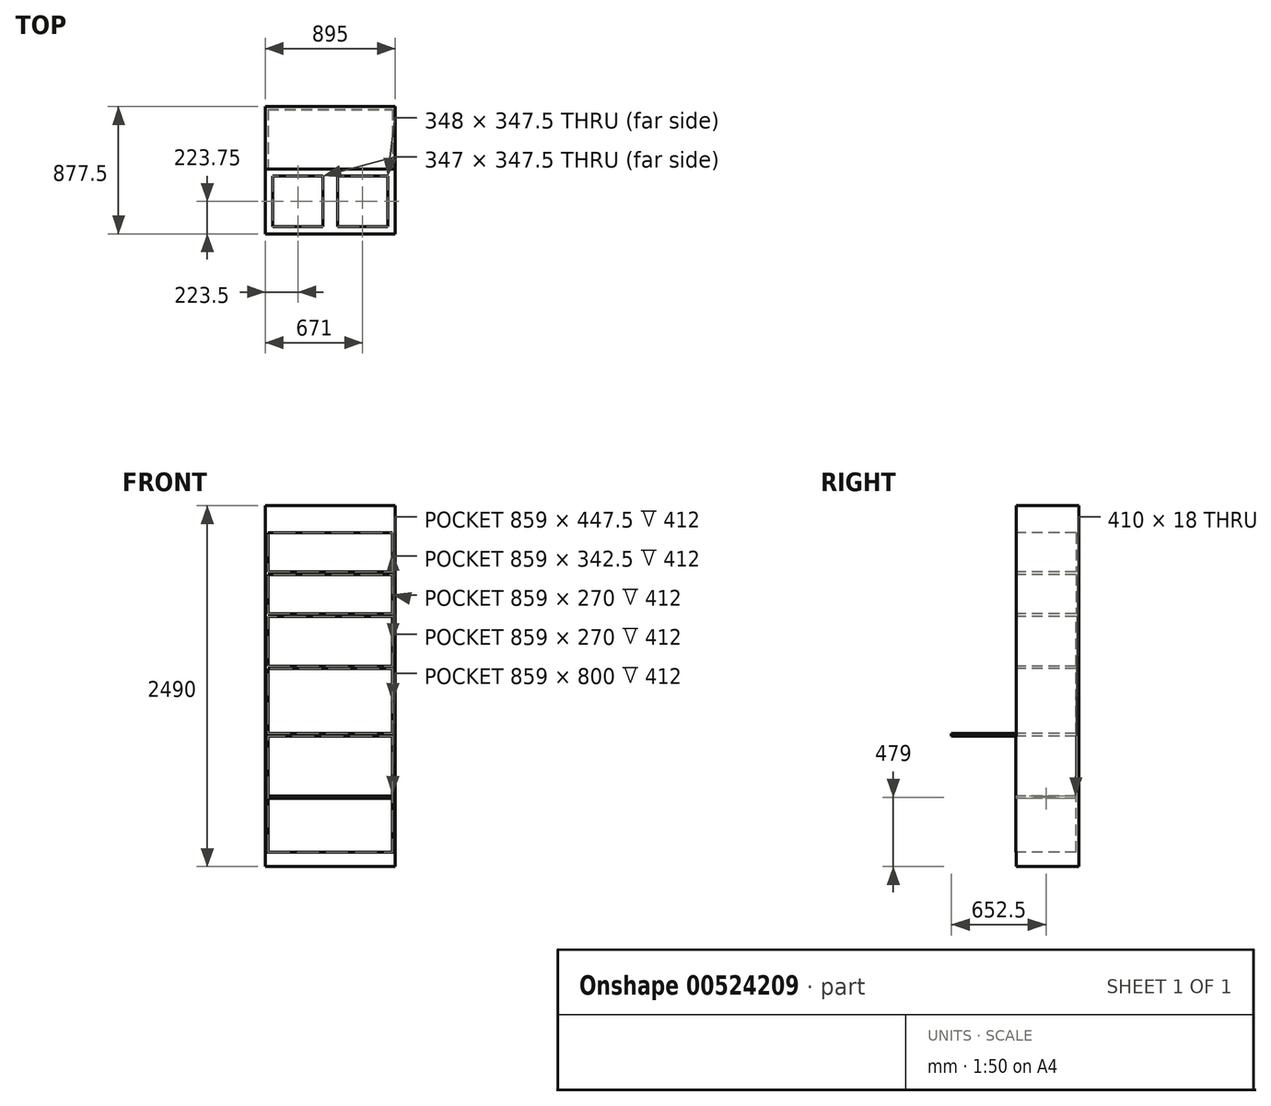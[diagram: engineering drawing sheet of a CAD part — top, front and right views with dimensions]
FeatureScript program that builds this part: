
annotation { "Feature Type Name" : "Feature", "Feature Type Description" : "" }
export const myFeature = defineFeature(function(context is Context, id is Id, definition is map)
    precondition{}
    {
        {
            var Q0;
            Q0=qCreatedBy(makeId("Top.planeOp"),FACE);
            var sketch = newSketch(context, id + "F0", { "sketchPlane" : qUnion([Q0])});
            skLineSegment(sketch, "E0.bottom", {"start": v(0, 0) * mm, "end": v(-1460, 0) * mm});
            skLineSegment(sketch, "E0.top", {"start": v(0, 650) * mm, "end": v(-1460, 650) * mm});
            skLineSegment(sketch, "E0.left", {"start": v(0, 0) * mm, "end": v(0, 650) * mm});
            skLineSegment(sketch, "E0.right", {"start": v(-1460, 0) * mm, "end": v(-1460, 650) * mm});
            skPoint(sketch, "E1.oppositeSnap0", {"position": v(-1460, 325) * mm});
            skLineSegment(sketch, "E1.bottom", {"start": v(-1460, 0) * mm, "end": v(-2355, 0) * mm});
            skLineSegment(sketch, "E1.left", {"start": v(-1460, 0) * mm, "end": v(-1460, 325) * mm});
            skLineSegment(sketch, "E1.right", {"start": v(-2355, 0) * mm, "end": v(-2355, 325) * mm});
            skLineSegment(sketch, "E2.bottom", {"start": v(-1460, 430) * mm, "end": v(-2355, 430) * mm});
            skLineSegment(sketch, "E2.left", {"start": v(-1460, 430) * mm, "end": v(-1460, 325) * mm});
            skLineSegment(sketch, "E2.right", {"start": v(-2355, 430) * mm, "end": v(-2355, 325) * mm});
            skSolve(sketch);
        }
        {
            var Q0;
            {var subQ0=sQuery(id+"F0.wireOp",EDGE,"E1.bottom");Q0=makeQuery(id+"F0.imprint","IMPRINT",FACE,{"disambiguationData":[TD([[makeQuery(id+"F0.imprint","IMPRINT",EDGE,{"derivedFrom":subQ0}),-1.0]])]});}
            extrude(context, id + "F1", {"entities" : qUnion([Q0]), "depth" : 2490 * mm, "offsetDistance" : 25 * mm});
        }
        {
            var Q0;
            Q0=makeQuery(id+"F1.opExtrude","SWEPT_FACE",FACE,{"disambiguationData":[OSD([sQuery(id+"F0.wireOp",EDGE,"E1.bottom")])]});
            var sketch = newSketch(context, id + "F2", { "sketchPlane" : qUnion([Q0])});
            skLineSegment(sketch, "E3.bottom", {"start": v(-2337, 2540) * mm, "end": v(-1478, 2540) * mm});
            skLineSegment(sketch, "E3.left", {"start": v(-2337, 2540) * mm, "end": v(-2337, 2320) * mm});
            skLineSegment(sketch, "E4.bottom", {"start": v(-2337, 2302) * mm, "end": v(-1478, 2302) * mm});
            skLineSegment(sketch, "E5.top", {"start": v(-2337, 100) * mm, "end": v(-1478, 100) * mm});
            skLineSegment(sketch, "E5.right", {"start": v(-1478, 2540) * mm, "end": v(-1478, 2320) * mm});
            skLineSegment(sketch, "E6", {"start": v(-2337, 2320) * mm, "end": v(-1478, 2320) * mm});
            skLineSegment(sketch, "E7.bottom", {"start": v(-1478, 2302) * mm, "end": v(-2337, 2302) * mm});
            skLineSegment(sketch, "E7.top", {"start": v(-1478, 2032) * mm, "end": v(-2337, 2032) * mm});
            skLineSegment(sketch, "E7.left", {"start": v(-1478, 2302) * mm, "end": v(-1478, 2032) * mm});
            skLineSegment(sketch, "E7.right", {"start": v(-2337, 2302) * mm, "end": v(-2337, 2032) * mm});
            skLineSegment(sketch, "E8.bottom", {"start": v(-1478, 100) * mm, "end": v(-1460, 100) * mm});
            skLineSegment(sketch, "E8.top", {"start": v(-1478, 900) * mm, "end": v(-1460, 900) * mm});
            skLineSegment(sketch, "E8.left", {"start": v(-1478, 100) * mm, "end": v(-1478, 900) * mm});
            skLineSegment(sketch, "E8.right", {"start": v(-1460, 100) * mm, "end": v(-1460, 900) * mm});
            skLineSegment(sketch, "E9.bottom", {"start": v(-2337, 100) * mm, "end": v(-2355, 100) * mm});
            skLineSegment(sketch, "E9.top", {"start": v(-2337, 900) * mm, "end": v(-2355, 900) * mm});
            skLineSegment(sketch, "E9.left", {"start": v(-2337, 100) * mm, "end": v(-2337, 900) * mm});
            skLineSegment(sketch, "E9.right", {"start": v(-2355, 100) * mm, "end": v(-2355, 900) * mm});
            skLineSegment(sketch, "E10.bottom", {"start": v(-2355, 900) * mm, "end": v(-1460, 900) * mm});
            skLineSegment(sketch, "E10.top", {"start": v(-2337, 918) * mm, "end": v(-1460, 918) * mm});
            skLineSegment(sketch, "E10.left", {"start": v(-2355, 900) * mm, "end": v(-2355, 918) * mm});
            skLineSegment(sketch, "E10.right", {"start": v(-1460, 900) * mm, "end": v(-1460, 918) * mm});
            skLineSegment(sketch, "E11.bottom", {"start": v(-2355, 918) * mm, "end": v(-1478, 918) * mm});
            skLineSegment(sketch, "E11.top", {"start": v(-2337, 1365.5) * mm, "end": v(-1478, 1365.5) * mm});
            skLineSegment(sketch, "E11.right", {"start": v(-1478, 918) * mm, "end": v(-1478, 1365.5) * mm});
            skLineSegment(sketch, "E12.bottom", {"start": v(-2337, 918) * mm, "end": v(-1478, 918) * mm});
            skLineSegment(sketch, "E12.left", {"start": v(-2337, 918) * mm, "end": v(-2337, 1365.5) * mm});
            skLineSegment(sketch, "E13.bottom", {"start": v(-2337, 2014) * mm, "end": v(-1478, 2014) * mm});
            skLineSegment(sketch, "E13.top", {"start": v(-2337, 1744) * mm, "end": v(-1478, 1744) * mm});
            skLineSegment(sketch, "E13.left", {"start": v(-2337, 2014) * mm, "end": v(-2337, 1744) * mm});
            skLineSegment(sketch, "E13.right", {"start": v(-1478, 2014) * mm, "end": v(-1478, 1744) * mm});
            skLineSegment(sketch, "E14.bottom", {"start": v(-2337, 1383.5) * mm, "end": v(-1478, 1383.5) * mm});
            skLineSegment(sketch, "E14.top", {"start": v(-2337, 1726) * mm, "end": v(-1478, 1726) * mm});
            skLineSegment(sketch, "E14.left", {"start": v(-2337, 1383.5) * mm, "end": v(-2337, 1726) * mm});
            skLineSegment(sketch, "E14.right", {"start": v(-1478, 1383.5) * mm, "end": v(-1478, 1726) * mm});
            skSolve(sketch);
        }
        {
            var Q0;
            Q0=makeQuery(id+"F2.imprint","IMPRINT",FACE,{"disambiguationData":[TD([[makeQuery(id+"F2.imprint","IMPRINT",EDGE,{"derivedFrom":sQuery(id+"F2.wireOp",EDGE,"E5.top")}),1.0]])]});
            var Q1;
            Q1=makeQuery(id+"F2.imprint","IMPRINT",FACE,{"disambiguationData":[TD([[makeQuery(id+"F2.imprint","IMPRINT",EDGE,{"derivedFrom":sQuery(id+"F2.wireOp",EDGE,"E11.top")}),-1.0]])]});
            var Q2;
            Q2=makeQuery(id+"F2.imprint","IMPRINT",FACE,{"disambiguationData":[TD([[makeQuery(id+"F2.imprint","IMPRINT",EDGE,{"derivedFrom":sQuery(id+"F2.wireOp",EDGE,"E14.bottom")}),1.0]])]});
            var Q3;
            Q3=makeQuery(id+"F2.imprint","IMPRINT",FACE,{"disambiguationData":[TD([[makeQuery(id+"F2.imprint","IMPRINT",EDGE,{"derivedFrom":sQuery(id+"F2.wireOp",EDGE,"E13.bottom")}),-1.0]])]});
            var Q4;
            {var subQ0=sQuery(id+"F2.wireOp",EDGE,"E3.bottom");Q4=makeQuery(id+"F2.imprint","IMPRINT",FACE,{"disambiguationData":[TD([[makeQuery(id+"F2.imprint","IMPRINT",EDGE,{"derivedFrom":subQ0}),-1.0]])]});}
            var Q5;
            Q5=makeQuery(id+"F2.imprint","IMPRINT",FACE,{"disambiguationData":[TD([[makeQuery(id+"F2.imprint","IMPRINT",EDGE,{"derivedFrom":sQuery(id+"F2.wireOp",EDGE,"E4.bottom")}),-1.0]])]});
            extrude(context, id + "F3", {"entities" : qUnion([Q0, Q1, Q2, Q3, Q4, Q5]), "operationType" : NewBodyOperationType.REMOVE, "oppositeDirection" : true, "depth" : 412 * mm, "offsetDistance" : 25 * mm});
        }
        {
            var Q0;
            Q0=makeQuery(id+"F2.imprint","IMPRINT",FACE,{"disambiguationData":[TD([[makeQuery(id+"F2.imprint","IMPRINT",EDGE,{"derivedFrom":sQuery(id+"F2.wireOp",EDGE,"E9.bottom")}),-1.0]])]});
            var Q1;
            Q1=makeQuery(id+"F2.imprint","IMPRINT",FACE,{"disambiguationData":[TD([[makeQuery(id+"F2.imprint","IMPRINT",EDGE,{"derivedFrom":sQuery(id+"F2.wireOp",EDGE,"E8.bottom")}),1.0]])]});
            extrude(context, id + "F4", {"entities" : qUnion([Q0, Q1]), "depth" : 89.5 / 20 * mm, "offsetDistance" : 25 * mm});
        }
        {
            var Q0;
            Q0=makeQuery(id+"F2.imprint","IMPRINT",FACE,{"disambiguationData":[TD([[makeQuery(id+"F2.imprint","IMPRINT",EDGE,{"derivedFrom":sQuery(id+"F2.wireOp",EDGE,"E8.top")}),1.0]])]});
            extrude(context, id + "F5", {"entities" : qUnion([Q0]), "depth" : 447.5 * mm, "offsetDistance" : 25 * mm});
        }
        {
            var Q0;
            Q0=makeQuery(id+"F4.opExtrude","SWEPT_FACE",FACE,{"disambiguationData":[OSD([sQuery(id+"F2.wireOp",EDGE,"E8.right")])]});
            var sketch = newSketch(context, id + "F6", { "sketchPlane" : qUnion([Q0])});
            skLineSegment(sketch, "E15.0.0", {"start": v(0, 100) * mm, "end": v(0, 900) * mm});
            skLineSegment(sketch, "E15.0.1", {"start": v(0, 900) * mm, "end": v(-447.5, 900) * mm});
            skLineSegment(sketch, "E15.0.2", {"start": v(-447.5, 900) * mm, "end": v(-447.5, 100) * mm});
            skLineSegment(sketch, "E15.0.3", {"start": v(-447.5, 100) * mm, "end": v(0, 100) * mm});
            skLineSegment(sketch, "E16.bottom", {"start": v(-397.5, 860) * mm, "end": v(-237.5, 860) * mm});
            skLineSegment(sketch, "E16.top", {"start": v(-397.5, 520) * mm, "end": v(-237.5, 520) * mm});
            skLineSegment(sketch, "E16.left", {"start": v(-397.5, 860) * mm, "end": v(-397.5, 520) * mm});
            skLineSegment(sketch, "E16.right", {"start": v(-237.5, 860) * mm, "end": v(-237.5, 520) * mm});
            skLineSegment(sketch, "E17.bottom", {"start": v(-207.5, 860) * mm, "end": v(-50, 860) * mm});
            skLineSegment(sketch, "E17.top", {"start": v(-207.5, 520) * mm, "end": v(-50, 520) * mm});
            skLineSegment(sketch, "E17.left", {"start": v(-207.5, 860) * mm, "end": v(-207.5, 520) * mm});
            skLineSegment(sketch, "E17.right", {"start": v(-50, 860) * mm, "end": v(-50, 520) * mm});
            skLineSegment(sketch, "E18.bottom", {"start": v(-397.5, 490) * mm, "end": v(-237.5, 490) * mm});
            skLineSegment(sketch, "E18.top", {"start": v(-397.5, 150) * mm, "end": v(-237.5, 150) * mm});
            skLineSegment(sketch, "E18.left", {"start": v(-397.5, 490) * mm, "end": v(-397.5, 150) * mm});
            skLineSegment(sketch, "E18.right", {"start": v(-237.5, 490) * mm, "end": v(-237.5, 150) * mm});
            skLineSegment(sketch, "E19.bottom", {"start": v(-207.5, 490) * mm, "end": v(-50, 490) * mm});
            skLineSegment(sketch, "E19.top", {"start": v(-207.5, 150) * mm, "end": v(-50, 150) * mm});
            skLineSegment(sketch, "E19.left", {"start": v(-207.5, 490) * mm, "end": v(-207.5, 150) * mm});
            skLineSegment(sketch, "E19.right", {"start": v(-50, 490) * mm, "end": v(-50, 150) * mm});
            skSolve(sketch);
        }
        {
            var Q0;
            Q0=makeQuery(id+"F6.imprint","IMPRINT",FACE,{"disambiguationData":[TD([[makeQuery(id+"F6.imprint","IMPRINT",EDGE,{"derivedFrom":sQuery(id+"F6.wireOp",EDGE,"E16.bottom")}),-1.0]])]});
            var Q1;
            Q1=makeQuery(id+"F6.imprint","IMPRINT",FACE,{"disambiguationData":[TD([[makeQuery(id+"F6.imprint","IMPRINT",EDGE,{"derivedFrom":sQuery(id+"F6.wireOp",EDGE,"E18.bottom")}),-1.0]])]});
            var Q2;
            Q2=makeQuery(id+"F6.imprint","IMPRINT",FACE,{"disambiguationData":[TD([[makeQuery(id+"F6.imprint","IMPRINT",EDGE,{"derivedFrom":sQuery(id+"F6.wireOp",EDGE,"E17.bottom")}),-1.0]])]});
            var Q3;
            Q3=makeQuery(id+"F6.imprint","IMPRINT",FACE,{"disambiguationData":[TD([[makeQuery(id+"F6.imprint","IMPRINT",EDGE,{"derivedFrom":sQuery(id+"F6.wireOp",EDGE,"E19.bottom")}),-1.0]])]});
            extrude(context, id + "F7", {"entities" : qUnion([Q0, Q1, Q2, Q3]), "operationType" : NewBodyOperationType.REMOVE, "oppositeDirection" : true, "depth" : 18 * mm, "offsetDistance" : 25 * mm});
        }
        {
            var Q0;
            Q0=makeQuery(id+"F4.opExtrude","SWEPT_FACE",FACE,{"disambiguationData":[OSD([sQuery(id+"F2.wireOp",EDGE,"E9.right")])]});
            var sketch = newSketch(context, id + "F8", { "sketchPlane" : qUnion([Q0])});
            skLineSegment(sketch, "E20.bottom", {"start": v(50, 860) * mm, "end": v(210, 860) * mm});
            skLineSegment(sketch, "E20.top", {"start": v(50, 520) * mm, "end": v(210, 520) * mm});
            skLineSegment(sketch, "E20.left", {"start": v(50, 860) * mm, "end": v(50, 520) * mm});
            skLineSegment(sketch, "E20.right", {"start": v(210, 860) * mm, "end": v(210, 520) * mm});
            skLineSegment(sketch, "E21.bottom", {"start": v(240, 860) * mm, "end": v(397.5, 860) * mm});
            skLineSegment(sketch, "E21.top", {"start": v(240, 520) * mm, "end": v(397.5, 520) * mm});
            skLineSegment(sketch, "E21.left", {"start": v(240, 860) * mm, "end": v(240, 520) * mm});
            skLineSegment(sketch, "E21.right", {"start": v(397.5, 860) * mm, "end": v(397.5, 520) * mm});
            skLineSegment(sketch, "E22.bottom", {"start": v(50, 490) * mm, "end": v(210, 490) * mm});
            skLineSegment(sketch, "E22.top", {"start": v(50, 150) * mm, "end": v(210, 150) * mm});
            skLineSegment(sketch, "E22.left", {"start": v(50, 490) * mm, "end": v(50, 150) * mm});
            skLineSegment(sketch, "E22.right", {"start": v(210, 490) * mm, "end": v(210, 150) * mm});
            skLineSegment(sketch, "E23.bottom", {"start": v(240, 490) * mm, "end": v(397.5, 490) * mm});
            skLineSegment(sketch, "E23.top", {"start": v(240, 150) * mm, "end": v(397.5, 150) * mm});
            skLineSegment(sketch, "E23.left", {"start": v(240, 490) * mm, "end": v(240, 150) * mm});
            skLineSegment(sketch, "E23.right", {"start": v(397.5, 490) * mm, "end": v(397.5, 150) * mm});
            skSolve(sketch);
        }
        {
            var Q0;
            Q0=makeQuery(id+"F8.imprint","IMPRINT",FACE,{"disambiguationData":[TD([[makeQuery(id+"F8.imprint","IMPRINT",EDGE,{"derivedFrom":sQuery(id+"F8.wireOp",EDGE,"E20.bottom")}),-1.0]])]});
            var Q1;
            Q1=makeQuery(id+"F8.imprint","IMPRINT",FACE,{"disambiguationData":[TD([[makeQuery(id+"F8.imprint","IMPRINT",EDGE,{"derivedFrom":sQuery(id+"F8.wireOp",EDGE,"E21.bottom")}),-1.0]])]});
            var Q2;
            Q2=makeQuery(id+"F8.imprint","IMPRINT",FACE,{"disambiguationData":[TD([[makeQuery(id+"F8.imprint","IMPRINT",EDGE,{"derivedFrom":sQuery(id+"F8.wireOp",EDGE,"E22.bottom")}),-1.0]])]});
            var Q3;
            Q3=makeQuery(id+"F8.imprint","IMPRINT",FACE,{"disambiguationData":[TD([[makeQuery(id+"F8.imprint","IMPRINT",EDGE,{"derivedFrom":sQuery(id+"F8.wireOp",EDGE,"E23.bottom")}),-1.0]])]});
            extrude(context, id + "F9", {"entities" : qUnion([Q0, Q1, Q2, Q3]), "operationType" : NewBodyOperationType.REMOVE, "oppositeDirection" : true, "depth" : 18 * mm, "offsetDistance" : 25 * mm});
        }
        {
            var Q0;
            Q0=makeQuery(id+"F2.imprint","IMPRINT",FACE,{"disambiguationData":[TD([[makeQuery(id+"F2.imprint","IMPRINT",EDGE,{"derivedFrom":sQuery(id+"F2.wireOp",EDGE,"E5.top")}),1.0]])]});
            var sketch = newSketch(context, id + "F10", { "sketchPlane" : qUnion([Q0])});
            skLineSegment(sketch, "E24.0", {"start": v(-2337, 470) * mm, "end": v(-2337, 488) * mm});
            skLineSegment(sketch, "E25.0", {"start": v(-1478, 470) * mm, "end": v(-1478, 488) * mm});
            skLineSegment(sketch, "E26.0", {"start": v(-2337, 100) * mm, "end": v(-1478, 100) * mm});
            skLineSegment(sketch, "E27.bottom", {"start": v(-2337, 488) * mm, "end": v(-1478, 488) * mm});
            skLineSegment(sketch, "E27.top", {"start": v(-2337, 470) * mm, "end": v(-1478, 470) * mm});
            skLineSegment(sketch, "E27.left", {"start": v(-2337, 488) * mm, "end": v(-2337, 470) * mm});
            skLineSegment(sketch, "E27.right", {"start": v(-1478, 488) * mm, "end": v(-1478, 470) * mm});
            skPoint(sketch, "E28.orphan", {"position": v(-1478, 900) * mm});
            skPoint(sketch, "E29.orphan", {"position": v(-2337, 900) * mm});
            skPoint(sketch, "E30.orphan", {"position": v(-2337, 100) * mm});
            skPoint(sketch, "E31.orphan", {"position": v(-1478, 100) * mm});
            skSolve(sketch);
        }
        {
            var Q0;
            Q0 = qSketchRegion(id + "F10", true);
            extrude(context, id + "F11", {"entities" : qUnion([Q0]), "operationType" : NewBodyOperationType.ADD, "oppositeDirection" : true, "depth" : 410 * mm, "offsetDistance" : 25 * mm});
        }
        {
            var Q0;
            Q0=makeQuery(id+"F5.opExtrude","SWEPT_FACE",FACE,{"disambiguationData":[OSD([sQuery(id+"F2.wireOp",EDGE,"E10.top"),sQuery(id+"F2.wireOp",EDGE,"E11.bottom")])]});
            var sketch = newSketch(context, id + "F12", { "sketchPlane" : qUnion([Q0])});
            skLineSegment(sketch, "E32.bottom", {"start": v(-2305, -50) * mm, "end": v(-1958, -50) * mm});
            skLineSegment(sketch, "E32.top", {"start": v(-2305, -397.5) * mm, "end": v(-1958, -397.5) * mm});
            skLineSegment(sketch, "E32.left", {"start": v(-2305, -50) * mm, "end": v(-2305, -397.5) * mm});
            skLineSegment(sketch, "E32.right", {"start": v(-1958, -50) * mm, "end": v(-1958, -397.5) * mm});
            skLineSegment(sketch, "E33.bottom", {"start": v(-1858, -50) * mm, "end": v(-1510, -50) * mm});
            skLineSegment(sketch, "E33.top", {"start": v(-1858, -397.5) * mm, "end": v(-1510, -397.5) * mm});
            skLineSegment(sketch, "E33.left", {"start": v(-1858, -50) * mm, "end": v(-1858, -397.5) * mm});
            skLineSegment(sketch, "E33.right", {"start": v(-1510, -50) * mm, "end": v(-1510, -397.5) * mm});
            skSolve(sketch);
        }
        {
            var Q0;
            Q0=makeQuery(id+"F12.imprint","IMPRINT",FACE,{"disambiguationData":[TD([[makeQuery(id+"F12.imprint","IMPRINT",EDGE,{"derivedFrom":sQuery(id+"F12.wireOp",EDGE,"E32.bottom")}),-1.0]])]});
            var Q1;
            Q1=makeQuery(id+"F12.imprint","IMPRINT",FACE,{"disambiguationData":[TD([[makeQuery(id+"F12.imprint","IMPRINT",EDGE,{"derivedFrom":sQuery(id+"F12.wireOp",EDGE,"E33.bottom")}),-1.0]])]});
            extrude(context, id + "F13", {"entities" : qUnion([Q0, Q1]), "operationType" : NewBodyOperationType.REMOVE, "oppositeDirection" : true, "depth" : 18 * mm, "offsetDistance" : 25 * mm});
        }
    });
